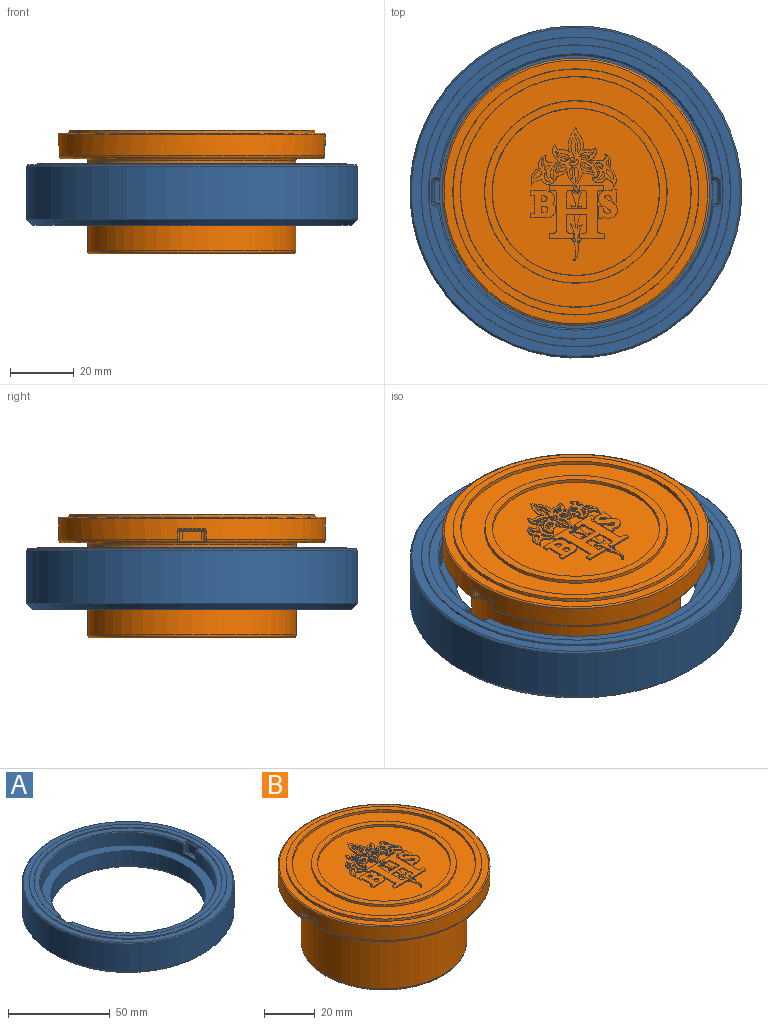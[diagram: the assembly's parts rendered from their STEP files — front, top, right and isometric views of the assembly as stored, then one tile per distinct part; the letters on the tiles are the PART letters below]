
ASSEMBLY  parts=2 mates=1
PART A: 47 faces, bbox 104.5x104.5x19.5 mm
  f0: plane 92.5x92.5mm, normal (0,0,1), area 739.9mm2, adj f2,f8,f12,f37,f38,f39,f40,f41
  f1: cylinder r=43mm len=86mm, axis (0,0,1), area 1938.4mm2, adj f2,f7,f8,f15,f16,f17,f21,f22
  f2: cone r=43mm half-angle=45deg, axis (0,0,1), area 90.1mm2, adj f0,f1,f41,f46
  f3: cylinder r=38.1mm len=76.2mm, axis (0,0,1), area 2154.5mm2, adj f7,f10
  f4: cylinder r=52.25mm len=104.5mm, axis (0,0,1), area 5416.9mm2, adj f9,f11
  f5: plane 100.5x100.5mm, normal (0,0,-1), area 2881mm2, adj f10,f11
  f6: plane 103.5x103.5mm, normal (0,0,1), area 947.2mm2, adj f9,f13
  f7: plane 86x86mm, normal (0,0,1), area 1248.4mm2, adj f1,f3
  f8: cone r=43mm half-angle=45deg, axis (0,0,1), area 90.1mm2, adj f0,f1,f37,f42
  f9: cone r=51.75mm half-angle=45deg, axis (0,0,-1), area 231mm2, adj f4,f6
  f10: cone r=40.1mm half-angle=45deg, axis (0,0,-1), area 694.9mm2, adj f3,f5
  f11: cone r=52.25mm half-angle=45deg, axis (0,0,1), area 910.8mm2, adj f4,f5
  f12: cone r=46.25mm half-angle=10deg, axis (0,0,1), area 147.7mm2, adj f0,f14
  f13: cone r=48.75mm half-angle=10deg, axis (0,0,-1), area 155.4mm2, adj f6,f14
  f14: plane 97.32x97.32mm, normal (0,0,1), area 693.5mm2, adj f12,f13
  f15: plane 7x1.64mm, normal (0,0,1), area 10.7mm2, adj f1,f27,f28,f29,f30,f31
  f16: plane 5x1.19mm, normal (0,-1,0), area 5.9mm2, adj f1,f18,f27,f42
  f17: plane 5x1.19mm, normal (0,1,0), area 5.9mm2, adj f1,f19,f31,f46
  f18: cylinder r=1mm len=5mm, axis (0,0,1), area 7.9mm2, adj f16,f20,f28,f43
  f19: cylinder r=1mm len=5mm, axis (0,0,1), area 7.9mm2, adj f17,f20,f30,f45
  f20: plane 6x5mm, normal (-1,0,0), area 30mm2, adj f18,f19,f29,f44
  f21: plane 7x1.64mm, normal (0,0,1), area 10.7mm2, adj f1,f32,f33,f34,f35,f36
  f22: plane 5x1.19mm, normal (0,1,0), area 5.9mm2, adj f1,f26,f36,f41
  f23: plane 5x1.19mm, normal (0,-1,0), area 5.9mm2, adj f1,f24,f32,f37
  f24: cylinder r=1mm len=5mm, axis (0,0,1), area 7.9mm2, adj f23,f25,f33,f38
  f25: plane 6x5mm, normal (1,0,0), area 30mm2, adj f24,f26,f34,f39
  f26: cylinder r=1mm len=5mm, axis (0,0,1), area 7.9mm2, adj f22,f25,f35,f40
  f27: cylinder r=0.5mm len=1.19mm, axis (-1,0,0), area 0.9mm2, adj f1,f15,f16,f28
  f28: torus R=0.5mm, axis (0,0,1), area 1mm2, adj f15,f18,f27,f29
  f29: cylinder r=0.5mm len=6mm, axis (0,1,0), area 4.7mm2, adj f15,f20,f28,f30
  f30: torus R=0.5mm, axis (0,0,1), area 1mm2, adj f15,f19,f29,f31
  f31: cylinder r=0.5mm len=1.19mm, axis (1,0,0), area 0.9mm2, adj f1,f15,f17,f30
  f32: cylinder r=0.5mm len=1.19mm, axis (-1,0,0), area 0.9mm2, adj f1,f21,f23,f33
  f33: torus R=0.5mm, axis (0,0,1), area 1mm2, adj f21,f24,f32,f34
  f34: cylinder r=0.5mm len=6mm, axis (0,-1,0), area 4.7mm2, adj f21,f25,f33,f35
  f35: torus R=0.5mm, axis (0,0,1), area 1mm2, adj f21,f26,f34,f36
  f36: cylinder r=0.5mm len=1.19mm, axis (1,0,0), area 0.9mm2, adj f1,f21,f22,f35
  f37: plane 1.19x0.5mm, normal (0,-0.71,0.71), area 0.7mm2, adj f0,f8,f23,f38
  f38: cone r=1mm half-angle=45deg, axis (0,0,1), area 1.4mm2, adj f0,f24,f37,f39
  f39: plane 6x0.5mm, normal (0.71,0,0.71), area 4.2mm2, adj f0,f25,f38,f40
  f40: cone r=1mm half-angle=45deg, axis (0,0,1), area 1.4mm2, adj f0,f26,f39,f41
  f41: plane 1.19x0.5mm, normal (0,0.71,0.71), area 0.7mm2, adj f0,f2,f22,f40
  f42: plane 1.19x0.5mm, normal (0,-0.71,0.71), area 0.7mm2, adj f0,f8,f16,f43
  f43: cone r=1mm half-angle=45deg, axis (0,0,1), area 1.4mm2, adj f0,f18,f42,f44
  f44: plane 6x0.5mm, normal (-0.71,0,0.71), area 4.2mm2, adj f0,f20,f43,f45
  f45: cone r=1mm half-angle=45deg, axis (0,0,1), area 1.4mm2, adj f0,f19,f44,f46
  f46: plane 1.19x0.5mm, normal (0,0.71,0.71), area 0.7mm2, adj f0,f2,f17,f45
PART B: 280 faces, bbox 90.9x90.9x39 mm
  f0: torus R=41mm, axis (0,0,-1), area 191.2mm2, adj f1,f3,f37,f50
  f1: cylinder r=42mm len=84mm, axis (0,0,-1), area 1652.3mm2, adj f0,f4,f5,f28,f31,f34,f36,f38
  f2: plane 83x83mm, normal (0,0,1), area 693.3mm2, adj f5,f60
  f3: plane 82x81.5mm, normal (0,0,-1), area 1764.8mm2, adj f0,f4,f9,f22,f25,f29,f32,f35
  f4: torus R=41mm, axis (0,0,-1), area 191.2mm2, adj f1,f3,f24,f49
  f5: torus R=41.5mm, axis (0,0,-1), area 206.4mm2, adj f1,f2
  f6: plane 63.6x63.6mm, normal (0,0,-1), area 534.8mm2, adj f7,f279
  f7: torus R=31.8mm, axis (0,0,-1), area 320.1mm2, adj f6,f8
  f8: cylinder r=32.8mm len=65.6mm, axis (0,0,-1), area 5873.5mm2, adj f7,f9
  f9: torus R=33.3mm, axis (0,0,-1), area 162.8mm2, adj f3,f8
  f10: plane 7x1.5mm, normal (0,0,-1), area 10mm2, adj f39,f40,f41,f42,f43,f44
  f11: plane 3x0.76mm, normal (0,-1,0), area 2.2mm2, adj f15,f42,f47,f49,f51
  f12: plane 3x0.76mm, normal (0,1,0), area 2.2mm2, adj f13,f44,f48,f50,f52
  f13: cylinder r=1mm len=3mm, axis (0,0,-1), area 4.7mm2, adj f12,f14,f41,f54
  f14: plane 6x3mm, normal (1,0,0), area 18mm2, adj f13,f15,f39,f55
  f15: cylinder r=1mm len=3mm, axis (0,0,-1), area 4.7mm2, adj f11,f14,f40,f53
  f16: plane 7x1.5mm, normal (0,0,-1), area 10mm2, adj f23,f26,f27,f30,f33,f34
  f17: plane 3x0.76mm, normal (0,-1,0), area 2.2mm2, adj f18,f22,f24,f27,f28
  f18: cylinder r=1mm len=3mm, axis (0,0,-1), area 4.7mm2, adj f17,f19,f23,f25
  f19: plane 6x3mm, normal (-1,0,0), area 18mm2, adj f18,f20,f26,f29
  f20: cylinder r=1mm len=3mm, axis (0,0,-1), area 4.7mm2, adj f19,f21,f30,f32
  f21: plane 3x0.76mm, normal (0,1,0), area 2.2mm2, adj f20,f33,f35,f37,f38
  f22: cylinder r=0.5mm len=0.5mm, axis (1,0,0), area 0.2mm2, adj f3,f17,f24,f25
  f23: torus R=0.5mm, axis (0,0,-1), area 1mm2, adj f16,f18,f26,f27
  f24: bspline ~1.28x1.24mm, area 1.1mm2, adj f4,f17,f22,f28
  f25: torus R=1.5mm, axis (0,0,1), area 1.5mm2, adj f3,f18,f22,f29
  f26: cylinder r=0.5mm len=6mm, axis (0,-1,0), area 4.7mm2, adj f16,f19,f23,f30
  f27: cylinder r=0.5mm len=0.85mm, axis (1,0,0), area 0.6mm2, adj f16,f17,f23,f31
  f28: cylinder r=0.5mm len=2.5mm, axis (0,0,-1), area 2.1mm2, adj f1,f17,f24,f31
  f29: cylinder r=0.5mm len=6mm, axis (0,-1,0), area 4.7mm2, adj f3,f19,f25,f32
  f30: torus R=0.5mm, axis (0,0,-1), area 1mm2, adj f16,f20,f26,f33
  f31: bspline ~1.22x1.18mm, area 0.9mm2, adj f1,f27,f28,f34
  f32: torus R=1.5mm, axis (0,0,1), area 1.5mm2, adj f3,f20,f29,f35
  f33: cylinder r=0.5mm len=0.85mm, axis (-1,0,0), area 0.6mm2, adj f16,f21,f30,f36
  f34: torus R=41.5mm, axis (0,0,-1), area 5.5mm2, adj f1,f16,f31,f36
  f35: cylinder r=0.5mm len=0.5mm, axis (-1,0,0), area 0.2mm2, adj f3,f21,f32,f37
  f36: bspline ~1.24x1.18mm, area 0.9mm2, adj f1,f33,f34,f38
  f37: bspline ~1.24x1.12mm, area 1.1mm2, adj f0,f21,f35,f38
  f38: cylinder r=0.5mm len=2.5mm, axis (0,0,-1), area 2.1mm2, adj f1,f21,f36,f37
  f39: cylinder r=0.5mm len=6mm, axis (0,1,0), area 4.7mm2, adj f10,f14,f40,f41
  f40: torus R=0.5mm, axis (0,0,-1), area 1mm2, adj f10,f15,f39,f42
  f41: torus R=0.5mm, axis (0,0,-1), area 1mm2, adj f10,f13,f39,f44
  f42: cylinder r=0.5mm len=0.85mm, axis (1,0,0), area 0.6mm2, adj f10,f11,f40,f45
  f43: torus R=41.5mm, axis (0,0,-1), area 5.5mm2, adj f1,f10,f45,f46
  f44: cylinder r=0.5mm len=0.85mm, axis (-1,0,0), area 0.6mm2, adj f10,f12,f41,f46
  f45: bspline ~1.24x1.18mm, area 0.9mm2, adj f1,f42,f43,f47
  f46: bspline ~1.22x1.18mm, area 0.9mm2, adj f1,f43,f44,f48
  f47: cylinder r=0.5mm len=2.5mm, axis (0,0,-1), area 2.1mm2, adj f1,f11,f45,f49
  f48: cylinder r=0.5mm len=2.5mm, axis (0,0,-1), area 2.1mm2, adj f1,f12,f46,f50
  f49: bspline ~1.24x1.12mm, area 1.1mm2, adj f4,f11,f47,f51
  f50: bspline ~1.28x1.24mm, area 1.1mm2, adj f0,f12,f48,f52
  f51: cylinder r=0.5mm len=0.5mm, axis (1,0,0), area 0.2mm2, adj f3,f11,f49,f53
  f52: cylinder r=0.5mm len=0.5mm, axis (-1,0,0), area 0.2mm2, adj f3,f12,f50,f54
  f53: torus R=1.5mm, axis (0,0,1), area 1.5mm2, adj f3,f15,f51,f55
  f54: torus R=1.5mm, axis (0,0,1), area 1.5mm2, adj f3,f13,f52,f55
  f55: cylinder r=0.5mm len=6mm, axis (0,1,0), area 4.7mm2, adj f3,f14,f53,f54
  f56: cylinder r=28mm len=56mm, axis (0,0,-1), area 4750.1mm2, adj f58,f279
  f57: plane 50x50mm, normal (0,0,-1), area 1963.5mm2, adj f58
  f58: torus R=25mm, axis (0,0,-1), area 796.8mm2, adj f56,f57
  f59: cone r=36.25mm half-angle=5deg, axis (0,0,1), area 228.9mm2, adj f61,f278
  f60: cone r=38.75mm half-angle=5deg, axis (0,0,-1), area 244.1mm2, adj f2,f61
  f61: plane 77.33x77.33mm, normal (0,0,1), area 547.8mm2, adj f59,f60
  f62: plane 1.95x0.81mm, normal (0,0,1), area 1.1mm2, adj f86,f87
  f63: plane 2.69x2.1mm, normal (0,0,1), area 1.9mm2, adj f88,f89,f90
  f64: plane 3.29x2.45mm, normal (0,0,1), area 3.7mm2, adj f91,f92,f93
  f65: plane 2.26x1.75mm, normal (0,0,1), area 2.1mm2, adj f94
  f66: plane 2.48x0.92mm, normal (0,0,1), area 1.3mm2, adj f95,f96,f97
  f67: plane 3.16x1.96mm, normal (0,0,1), area 2.5mm2, adj f98,f99,f100
  f68: plane 1.97x1.52mm, normal (0,0,1), area 1.6mm2, adj f101,f102,f103
  f69: plane 2.91x2.41mm, normal (0,0,1), area 3.8mm2, adj f104,f105,f106
  f70: plane 1.82x1.71mm, normal (0,0,1), area 2.8mm2, adj f107,f108,f109,f110
  f71: plane 2.04x1.92mm, normal (0,0,1), area 3.5mm2, adj f111,f112,f113,f114
  f72: plane 2.85x2.12mm, normal (0,0,1), area 2.9mm2, adj f115,f116
  f73: plane 3.54x1.82mm, normal (0,0,1), area 2.6mm2, adj f117,f118
  f74: plane 4.39x2.49mm, normal (0,0,1), area 3.2mm2, adj f119,f120,f121,f122
  f75: plane 3.85x1.14mm, normal (0,0,1), area 2.7mm2, adj f123,f124,f125
  f76: plane 5.53x1.56mm, normal (0,0,1), area 5.9mm2, adj f126,f127,f128
  f77: plane 4.47x2.34mm, normal (0,0,1), area 3.4mm2, adj f129,f130
  f78: plane 3.66x1.63mm, normal (0,0,1), area 2mm2, adj f131,f132,f133
  f79: plane 3.24x2.1mm, normal (0,0,1), area 1.7mm2, adj f134,f135,f136
  f80: plane 3.43x2.05mm, normal (0,0,1), area 2.6mm2, adj f137,f138,f139
  f81: plane 4.73x1.24mm, normal (0,0,1), area 4.3mm2, adj f140,f141,f142,f143,f144
  f82: plane 4.22x1.49mm, normal (0,0,1), area 3.1mm2, adj f145,f146
  f83: plane 2.78x1.06mm, normal (0,0,1), area 1.4mm2, adj f147,f148
  f84: plane 6.28x1.88mm, normal (0,0,1), area 4.3mm2, adj f149,f150
  f85: plane 1.24x1.24mm, normal (0,0,1), area 1.2mm2, adj f151
  f86: extruded ~1.95x0.5mm, area 1.1mm2, adj f62,f87,f153
  f87: extruded ~1.95x0.52mm, area 1.1mm2, adj f62,f86,f153
  f88: cylinder r=4.05mm len=2.69mm, axis (0,0,-1), area 1.6mm2, adj f63,f89,f90,f153
  f89: cylinder r=2.15mm len=2.07mm, axis (0,0,-1), area 1.3mm2, adj f63,f88,f90,f153
  f90: cylinder r=1.17mm len=1.25mm, axis (0,0,-1), area 0.7mm2, adj f63,f88,f89,f153
  f91: cylinder r=2.95mm len=2.5mm, axis (0,0,-1), area 1.8mm2, adj f64,f92,f93,f153
  f92: extruded ~3.29x2.4mm, area 2.2mm2, adj f64,f91,f93,f153
  f93: cylinder r=2.35mm len=0.8mm, axis (0,0,-1), area 0.4mm2, adj f64,f91,f92,f153
  f94: extruded ~2.24x1.73mm, area 3.4mm2, adj f65,f153
  f95: cylinder r=2.1mm len=2.48mm, axis (0,0,-1), area 1.3mm2, adj f66,f96,f97,f154
  f96: cylinder r=14.88mm len=0.82mm, axis (0,0,-1), area 0.5mm2, adj f66,f95,f97,f154
  f97: cylinder r=3.23mm len=1.66mm, axis (0,0,-1), area 0.8mm2, adj f66,f95,f96,f154
  f98: cylinder r=1.98mm len=1.96mm, axis (0,0,-1), area 1.5mm2, adj f67,f99,f100,f154
  f99: cylinder r=5.86mm len=3.16mm, axis (0,0,-1), area 1.7mm2, adj f67,f98,f100,f154
  f100: cylinder r=1.28mm len=1.2mm, axis (0,0,-1), area 0.7mm2, adj f67,f98,f99,f154
  f101: cylinder r=8.97mm len=1.96mm, axis (0,0,-1), area 1mm2, adj f68,f102,f103,f154
  f102: cylinder r=1.07mm len=1.16mm, axis (0,0,-1), area 0.7mm2, adj f68,f101,f103,f154
  f103: cylinder r=6.88mm len=1.52mm, axis (0,0,-1), area 1mm2, adj f68,f101,f102,f154
  f104: extruded ~2.91x2.39mm, area 2.1mm2, adj f69,f105,f106,f154
  f105: cylinder r=3.48mm len=2.28mm, axis (0,0,-1), area 1.7mm2, adj f69,f104,f106,f154
  f106: plane 0.63x0.5mm, normal (1,0,0), area 0.3mm2, adj f69,f104,f105,f154
  f107: plane 0.96x0.5mm, normal (0,-1,0), area 0.5mm2, adj f70,f108,f110,f157
  f108: plane 1.71x0.5mm, normal (1,0,0), area 0.9mm2, adj f70,f107,f109,f157
  f109: plane 0.96x0.5mm, normal (0,1,0), area 0.5mm2, adj f70,f108,f110,f157
  f110: cylinder r=0.86mm len=1.71mm, axis (0,0,-1), area 1.3mm2, adj f70,f107,f109,f157
  f111: plane 1.07x0.5mm, normal (0,-1,0), area 0.5mm2, adj f71,f112,f114,f157
  f112: plane 1.92x0.5mm, normal (1,0,0), area 1mm2, adj f71,f111,f113,f157
  f113: plane 1.16x0.5mm, normal (0,1,0), area 0.6mm2, adj f71,f112,f114,f157
  f114: cylinder r=0.96mm len=1.92mm, axis (0,0,-1), area 1.5mm2, adj f71,f111,f113,f157
  f115: cylinder r=2.11mm len=2.47mm, axis (0,0,-1), area 1.5mm2, adj f72,f116,f158
  f116: extruded ~2.84x2.11mm, area 2.5mm2, adj f72,f115,f158
  f117: extruded ~3.54x1.82mm, area 2.1mm2, adj f73,f118,f158
  f118: cylinder r=6.11mm len=3.54mm, axis (0,0,-1), area 2mm2, adj f73,f117,f158
  f119: cylinder r=1.66mm len=1.71mm, axis (0,0,-1), area 1.1mm2, adj f74,f120,f122,f158
  f120: extruded ~3.29x0.79mm, area 1.7mm2, adj f74,f119,f121,f158
  f121: extruded ~2.6x1.47mm, area 1.5mm2, adj f74,f120,f122,f158
  f122: cylinder r=3.91mm len=1.79mm, axis (0,0,-1), area 1mm2, adj f74,f119,f121,f158
  f123: cylinder r=3.97mm len=2.63mm, axis (0,0,-1), area 1.4mm2, adj f75,f124,f125,f158
  f124: cylinder r=25.91mm len=3.85mm, axis (0,0,-1), area 1.9mm2, adj f75,f123,f125,f158
  f125: cylinder r=1.26mm len=1.21mm, axis (0,0,-1), area 0.9mm2, adj f75,f123,f124,f158
  f126: cylinder r=5.61mm len=5.53mm, axis (0,0,-1), area 2.9mm2, adj f76,f127,f128,f158
  f127: cylinder r=5.82mm len=4.5mm, axis (0,0,-1), area 2.3mm2, adj f76,f126,f128,f158
  f128: extruded ~1.03x0.71mm, area 0.6mm2, adj f76,f126,f127,f158
  f129: extruded ~4.47x2.34mm, area 2.7mm2, adj f77,f130,f158
  f130: extruded ~4.47x2.34mm, area 2.6mm2, adj f77,f129,f158
  f131: cylinder r=1.71mm len=1.88mm, axis (0,0,-1), area 1mm2, adj f78,f132,f133,f158
  f132: cylinder r=12.58mm len=3.66mm, axis (0,0,-1), area 1.9mm2, adj f78,f131,f133,f158
  f133: extruded ~1.79x1.49mm, area 1.2mm2, adj f78,f131,f132,f158
  f134: cylinder r=2.28mm len=2.06mm, axis (0,0,-1), area 1.5mm2, adj f79,f135,f136,f158
  f135: cylinder r=5.2mm len=3.24mm, axis (0,0,-1), area 1.9mm2, adj f79,f134,f136,f158
  f136: cylinder r=2.87mm len=1.48mm, axis (0,0,-1), area 0.8mm2, adj f79,f134,f135,f158
  f137: cylinder r=1.72mm len=0.57mm, axis (0,0,-1), area 0.3mm2, adj f80,f138,f139,f158
  f138: cylinder r=4.06mm len=2.85mm, axis (0,0,-1), area 1.8mm2, adj f80,f137,f139,f158
  f139: extruded ~3.43x2.02mm, area 2.1mm2, adj f80,f137,f138,f158
  f140: cylinder r=3.09mm len=2.66mm, axis (0,0,-1), area 1.4mm2, adj f81,f141,f144,f158
  f141: plane 0.5x0.48mm, normal (0.03,-1,0), area 0.2mm2, adj f81,f140,f142,f158
  f142: cylinder r=36.37mm len=4.15mm, axis (0,0,-1), area 2.1mm2, adj f81,f141,f143,f158
  f143: cylinder r=1.5mm len=0.57mm, axis (0,0,-1), area 0.3mm2, adj f81,f142,f144,f158
  f144: cylinder r=6.63mm len=2.07mm, axis (0,0,-1), area 1.1mm2, adj f81,f140,f143,f158
  f145: extruded ~4.22x1.49mm, area 2.4mm2, adj f82,f146,f158
  f146: extruded ~4.22x1.49mm, area 2.4mm2, adj f82,f145,f158
  f147: extruded ~2.78x1.04mm, area 1.6mm2, adj f83,f148,f158
  f148: extruded ~2.78x1.04mm, area 1.6mm2, adj f83,f147,f158
  f149: extruded ~6.28x1.85mm, area 3.5mm2, adj f84,f150,f158
  f150: extruded ~6.28x1.26mm, area 3.2mm2, adj f84,f149,f158
  f151: cylinder r=0.62mm len=1.24mm, axis (0,0,-1), area 2mm2, adj f85,f158
  f152: plane 14.39x3.77mm, normal (0,0,1), area 18mm2, adj f160,f161,f162,f163,f164,f165,f166,f167
  f153: plane 10.23x8.23mm, normal (0,0,1), area 30.2mm2, adj f86,f87,f88,f89,f90,f91,f92,f93
  f154: plane 9.72x8.28mm, normal (0,0,1), area 29.4mm2, adj f95,f96,f97,f98,f99,f100,f101,f102
  f155: plane 9.07x6.06mm, normal (0,0,1), area 39.9mm2, adj f183,f184,f185,f186,f187,f188,f189,f190
  f156: plane 17.25x16.63mm, normal (0,0,1), area 151.1mm2, adj f200,f201,f202,f203,f204,f205,f206,f207
  f157: plane 8.51x7.81mm, normal (0,0,1), area 49.1mm2, adj f107,f108,f109,f110,f111,f112,f113,f114
  f158: plane 18.91x14.15mm, normal (0,0,1), area 90.5mm2, adj f115,f116,f117,f118,f119,f120,f121,f122
  f159: plane 6.18x3.58mm, normal (0,0,1), area 9.2mm2, adj f262,f263,f264,f265,f266,f267,f268,f269
  f160: extruded ~1.49x1.18mm, area 1mm2, adj f152,f161,f170,f274
  f161: cylinder r=13.93mm len=5.77mm, axis (0,0,-1), area 3mm2, adj f152,f160,f162,f274
  f162: cylinder r=2.61mm len=1.03mm, axis (0,0,-1), area 0.6mm2, adj f152,f161,f163,f274
  f163: extruded ~6.41x1.23mm, area 3.5mm2, adj f152,f162,f164,f274
  f164: extruded ~6.4x2.8mm, area 3.9mm2, adj f152,f163,f165,f274
  f165: cylinder r=1.36mm len=1.13mm, axis (0,0,-1), area 0.7mm2, adj f152,f164,f166,f274
  f166: cylinder r=10.01mm len=5.67mm, axis (0,0,-1), area 3mm2, adj f152,f165,f167,f274
  f167: cylinder r=2.56mm len=1.6mm, axis (0,0,-1), area 1.1mm2, adj f152,f166,f168,f274
  f168: cylinder r=16.54mm len=4.48mm, axis (0,0,-1), area 2.3mm2, adj f152,f167,f169,f274
  f169: plane 1.82x0.5mm, normal (0,1,0), area 0.9mm2, adj f152,f168,f170,f274
  f170: cylinder r=20.41mm len=3.96mm, axis (0,0,-1), area 2mm2, adj f152,f160,f169,f274
  f171: extruded ~4.48x1.58mm, area 3mm2, adj f153,f172,f176,f274
  f172: extruded ~2.88x2.08mm, area 1.9mm2, adj f153,f171,f173,f274
  f173: extruded ~6.26x2.13mm, area 3.6mm2, adj f153,f172,f174,f274
  f174: extruded ~3.97x1.89mm, area 2.5mm2, adj f153,f173,f175,f274
  f175: extruded ~4.79x2.11mm, area 3.2mm2, adj f153,f174,f176,f274
  f176: extruded ~5.3x2.83mm, area 3.9mm2, adj f153,f171,f175,f274
  f177: extruded ~5.93x2.19mm, area 3.6mm2, adj f154,f178,f182,f274
  f178: extruded ~3.66x2.41mm, area 2.8mm2, adj f154,f177,f179,f274
  f179: extruded ~4.08x2.48mm, area 2.6mm2, adj f154,f178,f180,f274
  f180: extruded ~5.64x2.6mm, area 3.4mm2, adj f154,f179,f181,f274
  f181: cylinder r=4.01mm len=3.29mm, axis (0,0,-1), area 2mm2, adj f154,f180,f182,f274
  f182: cylinder r=2.28mm len=4.07mm, axis (0,0,-1), area 2.5mm2, adj f154,f177,f181,f274
  f183: cylinder r=2.53mm len=4mm, axis (0,0,-1), area 2.3mm2, adj f155,f184,f199,f274
  f184: extruded ~2.6x2.41mm, area 3.5mm2, adj f155,f183,f185,f274
  f185: plane 0.5x0.22mm, normal (-0.62,-0.78,0), area 0.1mm2, adj f155,f184,f186,f274
  f186: plane 1.11x0.5mm, normal (0,-1,0), area 0.6mm2, adj f155,f185,f187,f274
  f187: plane 3.91x0.5mm, normal (1,0,0), area 2mm2, adj f155,f186,f188,f274
  f188: plane 1.28x0.5mm, normal (0,1,0), area 0.6mm2, adj f155,f187,f189,f274
  f189: plane 0.61x0.5mm, normal (-1,0,0), area 0.3mm2, adj f155,f188,f190,f274
  f190: cylinder r=2.75mm len=3.68mm, axis (0,0,-1), area 2mm2, adj f155,f189,f191,f274
  f191: cylinder r=2.38mm len=3.47mm, axis (0,0,-1), area 1.9mm2, adj f155,f190,f192,f274
  f192: cylinder r=9.45mm len=1.8mm, axis (0,0,-1), area 1.1mm2, adj f155,f191,f193,f274
  f193: extruded ~2.37x2.12mm, area 2.9mm2, adj f155,f192,f194,f274
  f194: plane 1.39x0.5mm, normal (0,1,0), area 0.7mm2, adj f155,f193,f195,f274
  f195: plane 3.86x0.5mm, normal (-1,0,0), area 1.9mm2, adj f155,f194,f196,f274
  f196: plane 1.4x0.5mm, normal (0,-1,0), area 0.7mm2, adj f155,f195,f197,f274
  f197: plane 0.58x0.5mm, normal (1,0,0), area 0.3mm2, adj f155,f196,f198,f274
  f198: plane 0.52x0.5mm, normal (-0.38,-0.93,0), area 0.3mm2, adj f155,f197,f199,f274
  f199: cylinder r=3.18mm len=3.32mm, axis (0,0,-1), area 1.8mm2, adj f155,f183,f198,f274
  f200: plane 1.5x0.5mm, normal (0,-1,0), area 0.8mm2, adj f156,f201,f235,f274
  f201: cylinder r=0.7mm len=0.7mm, axis (0,0,-1), area 0.5mm2, adj f156,f200,f202,f274
  f202: plane 4.87x0.5mm, normal (-1,0,0), area 2.4mm2, adj f156,f201,f203,f274
  f203: plane 6.33x0.5mm, normal (0,1,0), area 3.2mm2, adj f156,f202,f204,f274
  f204: plane 4.87x0.5mm, normal (1,0,0), area 2.4mm2, adj f156,f203,f205,f274
  f205: cylinder r=0.7mm len=0.7mm, axis (0,0,-1), area 0.5mm2, adj f156,f204,f206,f274
  f206: plane 1.38x0.5mm, normal (0,-1,0), area 0.7mm2, adj f156,f205,f207,f274
  f207: plane 1.68x0.5mm, normal (1,0,0), area 0.8mm2, adj f156,f206,f208,f274
  f208: plane 7.57x0.5mm, normal (0,1,0), area 3.8mm2, adj f156,f207,f209,f274
  f209: plane 1.68x0.5mm, normal (-1,0,0), area 0.8mm2, adj f156,f208,f210,f274
  f210: plane 1.46x0.5mm, normal (0,-1,0), area 0.7mm2, adj f156,f209,f211,f274
  f211: cylinder r=0.7mm len=0.7mm, axis (0,0,-1), area 0.5mm2, adj f156,f210,f212,f274
  f212: plane 11.96x0.5mm, normal (-1,0,0), area 6mm2, adj f156,f211,f213,f274
  f213: cylinder r=0.7mm len=0.7mm, axis (0,0,-1), area 0.5mm2, adj f156,f212,f214,f274
  f214: plane 1.46x0.5mm, normal (0,1,0), area 0.7mm2, adj f156,f213,f215,f274
  f215: plane 1.58x0.5mm, normal (-1,0,0), area 0.8mm2, adj f156,f214,f216,f274
  f216: plane 7.57x0.5mm, normal (0,-1,0), area 3.8mm2, adj f156,f215,f217,f274
  f217: plane 1.58x0.5mm, normal (1,0,0), area 0.8mm2, adj f156,f216,f218,f274
  f218: plane 1.38x0.5mm, normal (0,1,0), area 0.7mm2, adj f156,f217,f219,f274
  f219: cylinder r=0.7mm len=0.7mm, axis (0,0,-1), area 0.5mm2, adj f156,f218,f220,f274
  f220: plane 5.12x0.5mm, normal (1,0,0), area 2.6mm2, adj f156,f219,f221,f274
  f221: plane 6.33x0.5mm, normal (0,-1,0), area 3.2mm2, adj f156,f220,f222,f274
  f222: plane 5.12x0.5mm, normal (-1,0,0), area 2.6mm2, adj f156,f221,f223,f274
  f223: cylinder r=0.7mm len=0.7mm, axis (0,0,-1), area 0.5mm2, adj f156,f222,f224,f274
  f224: plane 1.5x0.5mm, normal (0,1,0), area 0.8mm2, adj f156,f223,f225,f274
  f225: plane 1.58x0.5mm, normal (-1,0,0), area 0.8mm2, adj f156,f224,f226,f274
  f226: plane 7.63x0.5mm, normal (0,-1,0), area 3.8mm2, adj f156,f225,f227,f274
  f227: plane 1.58x0.5mm, normal (1,0,0), area 0.8mm2, adj f156,f226,f228,f274
  f228: plane 1.45x0.5mm, normal (0,1,0), area 0.7mm2, adj f156,f227,f229,f274
  f229: cylinder r=0.7mm len=0.7mm, axis (0,0,-1), area 0.5mm2, adj f156,f228,f230,f274
  f230: plane 11.96x0.5mm, normal (1,0,0), area 6mm2, adj f156,f229,f231,f274
  f231: cylinder r=0.7mm len=0.7mm, axis (0,0,-1), area 0.5mm2, adj f156,f230,f232,f274
  f232: plane 1.33x0.5mm, normal (0,-1,0), area 0.7mm2, adj f156,f231,f233,f274
  f233: plane 1.68x0.5mm, normal (1,0,0), area 0.8mm2, adj f156,f232,f234,f274
  f234: plane 7.52x0.5mm, normal (0,1,0), area 3.8mm2, adj f156,f233,f235,f274
  f235: plane 1.68x0.5mm, normal (-1,0,0), area 0.8mm2, adj f156,f200,f234,f274
  f236: cylinder r=2.36mm len=3.74mm, axis (0,0,-1), area 2.2mm2, adj f157,f237,f246,f274
  f237: extruded ~1.67x0.5mm, area 0.9mm2, adj f157,f236,f238,f274
  f238: plane 4.35x0.5mm, normal (0,1,0), area 2.2mm2, adj f157,f237,f239,f274
  f239: plane 1.53x0.5mm, normal (-1,0,0), area 0.8mm2, adj f157,f238,f240,f274
  f240: plane 1.02x0.5mm, normal (0,-1,0), area 0.5mm2, adj f157,f239,f241,f274
  f241: plane 5.65x0.5mm, normal (-1,0,0), area 2.8mm2, adj f157,f240,f242,f274
  f242: plane 1.02x0.5mm, normal (0,1,0), area 0.5mm2, adj f157,f241,f243,f274
  f243: plane 1.33x0.5mm, normal (-1,0,0), area 0.7mm2, adj f157,f242,f244,f274
  f244: plane 5.03x0.5mm, normal (0,-1,0), area 2.5mm2, adj f157,f243,f245,f274
  f245: extruded ~1.31x0.5mm, area 0.7mm2, adj f157,f244,f246,f274
  f246: cylinder r=2.42mm len=4.11mm, axis (0,0,-1), area 2.5mm2, adj f157,f236,f245,f274
  f247: extruded ~7.74x2.42mm, area 4.2mm2, adj f158,f248,f261,f274
  f248: extruded ~3.87x0.95mm, area 2.1mm2, adj f158,f247,f249,f274
  f249: extruded ~1.43x0.82mm, area 0.8mm2, adj f158,f248,f250,f274
  f250: extruded ~5.61x2.39mm, area 3.3mm2, adj f158,f249,f251,f274
  f251: cylinder r=2.95mm len=1.89mm, axis (0,0,-1), area 1.3mm2, adj f158,f250,f252,f274
  f252: extruded ~3.88x0.92mm, area 2.1mm2, adj f158,f251,f253,f274
  f253: extruded ~1.06x0.5mm, area 0.5mm2, adj f158,f252,f254,f274
  f254: extruded ~3.47x1.71mm, area 1.9mm2, adj f158,f253,f255,f274
  f255: extruded ~5.22x2.75mm, area 3mm2, adj f158,f254,f256,f274
  f256: extruded ~4.75x1.92mm, area 2.6mm2, adj f158,f255,f257,f274
  f257: extruded ~3.85x1.5mm, area 2.2mm2, adj f158,f256,f258,f274
  f258: extruded ~5.25x3.36mm, area 3.6mm2, adj f158,f257,f259,f274
  f259: extruded ~4.14x2.96mm, area 2.9mm2, adj f158,f258,f260,f274
  f260: extruded ~4.29x0.94mm, area 2.3mm2, adj f158,f259,f261,f274
  f261: extruded ~7.24x2.44mm, area 4mm2, adj f158,f247,f260,f274
  f262: cylinder r=19.07mm len=5.31mm, axis (0,0,-1), area 2.7mm2, adj f159,f263,f273,f274
  f263: cylinder r=2.62mm len=1.2mm, axis (0,0,-1), area 0.8mm2, adj f159,f262,f264,f274
  f264: cylinder r=2.79mm len=1.67mm, axis (0,0,-1), area 0.8mm2, adj f159,f263,f265,f274
  f265: cylinder r=2.93mm len=1.18mm, axis (0,0,-1), area 0.6mm2, adj f159,f264,f266,f274
  f266: cylinder r=11.83mm len=0.8mm, axis (0,0,-1), area 0.4mm2, adj f159,f265,f267,f274
  f267: cylinder r=1.31mm len=1.18mm, axis (0,0,-1), area 0.6mm2, adj f159,f266,f268,f274
  f268: cylinder r=1.84mm len=1.17mm, axis (0,0,-1), area 0.7mm2, adj f159,f267,f269,f274
  f269: extruded ~4.91x1.7mm, area 3.4mm2, adj f159,f268,f270,f274
  f270: cylinder r=51.88mm len=0.94mm, axis (0,0,-1), area 0.5mm2, adj f159,f269,f271,f274
  f271: plane 2.85x0.5mm, normal (0,-1,0), area 1.4mm2, adj f159,f270,f272,f274
  f272: cylinder r=4.73mm len=0.72mm, axis (0,0,-1), area 0.4mm2, adj f159,f271,f273,f274
  f273: cylinder r=1.82mm len=1.36mm, axis (0,0,-1), area 0.8mm2, adj f159,f262,f272,f274
  f274: plane 52.5x52.5mm, normal (0,0,1), area 1681.6mm2, adj f160,f161,f162,f163,f164,f165,f166,f167
  f275: cone r=26.25mm half-angle=5deg, axis (0,0,1), area 165.8mm2, adj f274,f276
  f276: plane 57.33x57.33mm, normal (0,0,1), area 401.7mm2, adj f275,f277
  f277: cone r=28.75mm half-angle=5deg, axis (0,0,-1), area 181.1mm2, adj f276,f278
  f278: plane 72.5x72.5mm, normal (0,0,1), area 1531.5mm2, adj f59,f277
  f279: cone r=28mm half-angle=45deg, axis (0,0,-1), area 253.2mm2, adj f6,f56
PLACE A t=(-10.77,-4.18,-11.45)mm
PLACE B t=(-10.77,-4.18,-39.45)mm
MATE parallel B.f0 <-> A.f4  axis (0,0,-1) through (-10.77,-4.18,-9.45)mm
